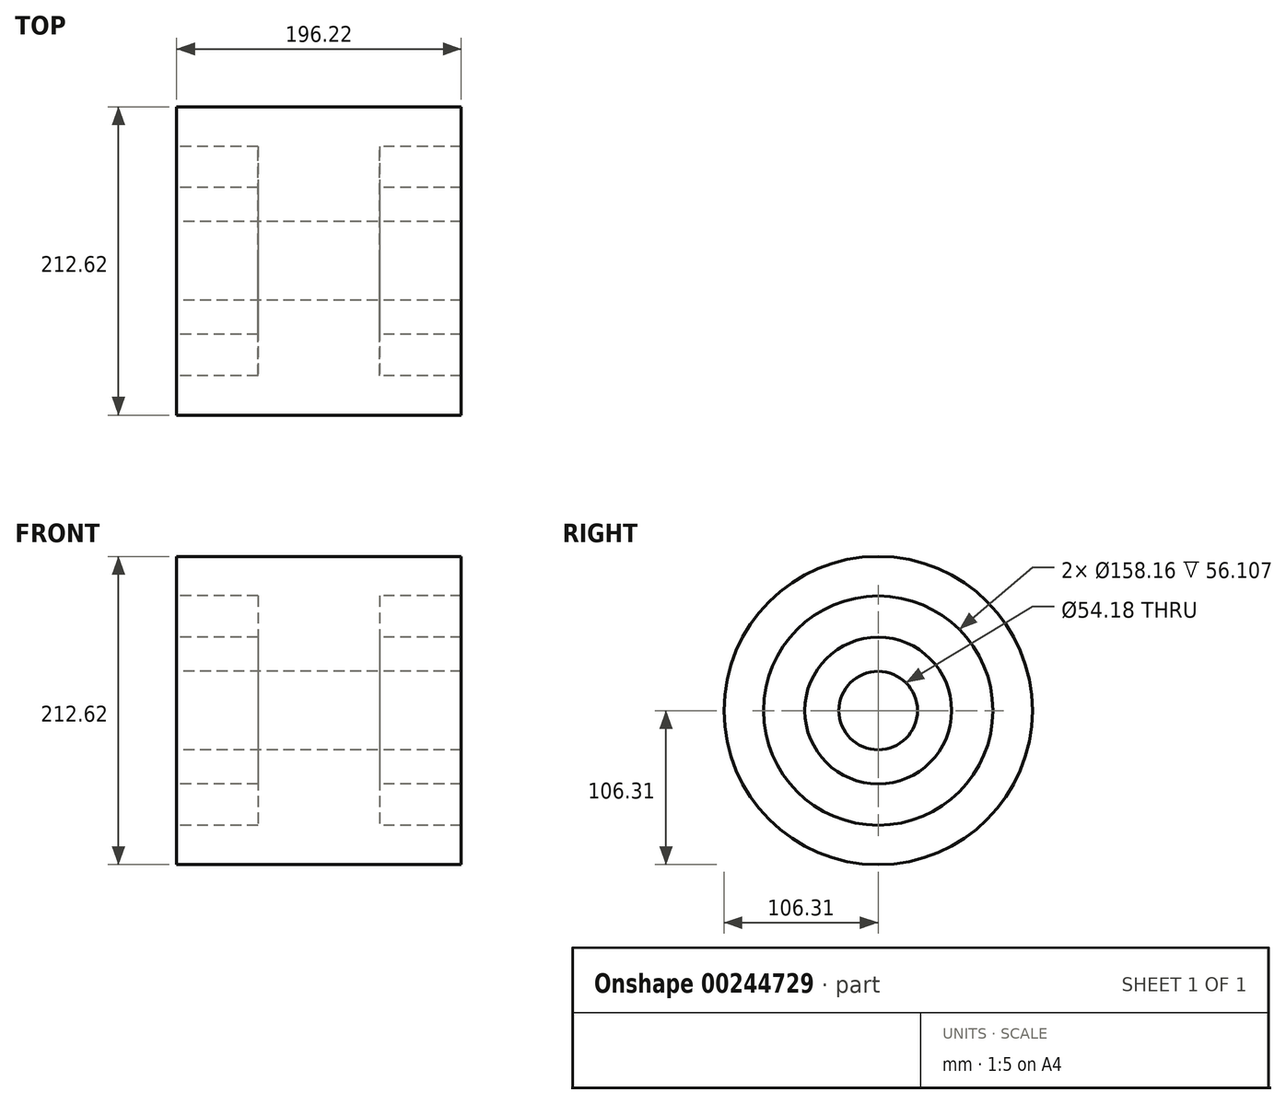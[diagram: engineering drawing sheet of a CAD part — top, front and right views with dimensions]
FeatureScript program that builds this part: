
annotation { "Feature Type Name" : "Feature", "Feature Type Description" : "" }
export const myFeature = defineFeature(function(context is Context, id is Id, definition is map)
    precondition{}
    {
        {
            var Q0;
            Q0=qCreatedBy(makeId("Front.planeOp"),FACE);
            var sketch = newSketch(context, id + "F0", { "sketchPlane" : qUnion([Q0])});
            skLineSegment(sketch, "E0", {"start": v(-120.51, 0) * mm, "end": v(116.43, 0) * mm});
            skLineSegment(sketch, "E1", {"start": v(0, 0) * mm, "end": v(0, 143.86) * mm});
            skLineSegment(sketch, "E2", {"start": v(0, 106.3) * mm, "end": v(98.11, 106.3) * mm});
            skLineSegment(sketch, "E3", {"start": v(98.11, 106.3) * mm, "end": v(98.11, 79.08) * mm});
            skLineSegment(sketch, "E4", {"start": v(98.11, 79.08) * mm, "end": v(42, 79.08) * mm});
            skLineSegment(sketch, "E5", {"start": v(42, 79.08) * mm, "end": v(42, 50.6) * mm});
            skLineSegment(sketch, "E6", {"start": v(42, 50.6) * mm, "end": v(98.11, 50.6) * mm});
            skLineSegment(sketch, "E7", {"start": v(98.11, 50.6) * mm, "end": v(98.11, 27.09) * mm});
            skLineSegment(sketch, "E8", {"start": v(98.11, 27.09) * mm, "end": v(0, 27.09) * mm});
            skLineSegment(sketch, "E9.MirrorCS", {"start": v(0, 106.3) * mm, "end": v(-98.11, 106.3) * mm});
            skLineSegment(sketch, "E10.MirrorCS", {"start": v(-98.11, 106.3) * mm, "end": v(-98.11, 79.08) * mm});
            skLineSegment(sketch, "E11.MirrorCS", {"start": v(-98.11, 79.08) * mm, "end": v(-42, 79.08) * mm});
            skLineSegment(sketch, "E12.MirrorCS", {"start": v(-42, 79.08) * mm, "end": v(-42, 50.6) * mm});
            skLineSegment(sketch, "E13.MirrorCS", {"start": v(-42, 50.6) * mm, "end": v(-98.11, 50.6) * mm});
            skLineSegment(sketch, "E14.MirrorCS", {"start": v(-98.11, 50.6) * mm, "end": v(-98.11, 27.09) * mm});
            skLineSegment(sketch, "E15.MirrorCS", {"start": v(-98.11, 27.09) * mm, "end": v(0, 27.09) * mm});
            skSolve(sketch);
        }
        {
            var Q0;
            {var subQ0=sQuery(id+"F0.wireOp",EDGE,"E2");Q0=makeQuery(id+"F0.imprint","IMPRINT",FACE,{"disambiguationData":[TD([[makeQuery(id+"F0.imprint","IMPRINT",EDGE,{"derivedFrom":subQ0}),-1.0]])]});}
            var Q1;
            {var subQ0=sQuery(id+"F0.wireOp",EDGE,"E9.MirrorCS");Q1=makeQuery(id+"F0.imprint","IMPRINT",FACE,{"disambiguationData":[TD([[makeQuery(id+"F0.imprint","IMPRINT",EDGE,{"derivedFrom":subQ0}),1.0]])]});}
            var Q2;
            Q2=sQuery(id+"F0.wireOp",EDGE,"E0");
            revolve(context, id + "F1", {"entities" : qUnion([Q0, Q1]), "axis" : qUnion([Q2]), "revolveType" : RevolveType.FULL});
        }
    });
